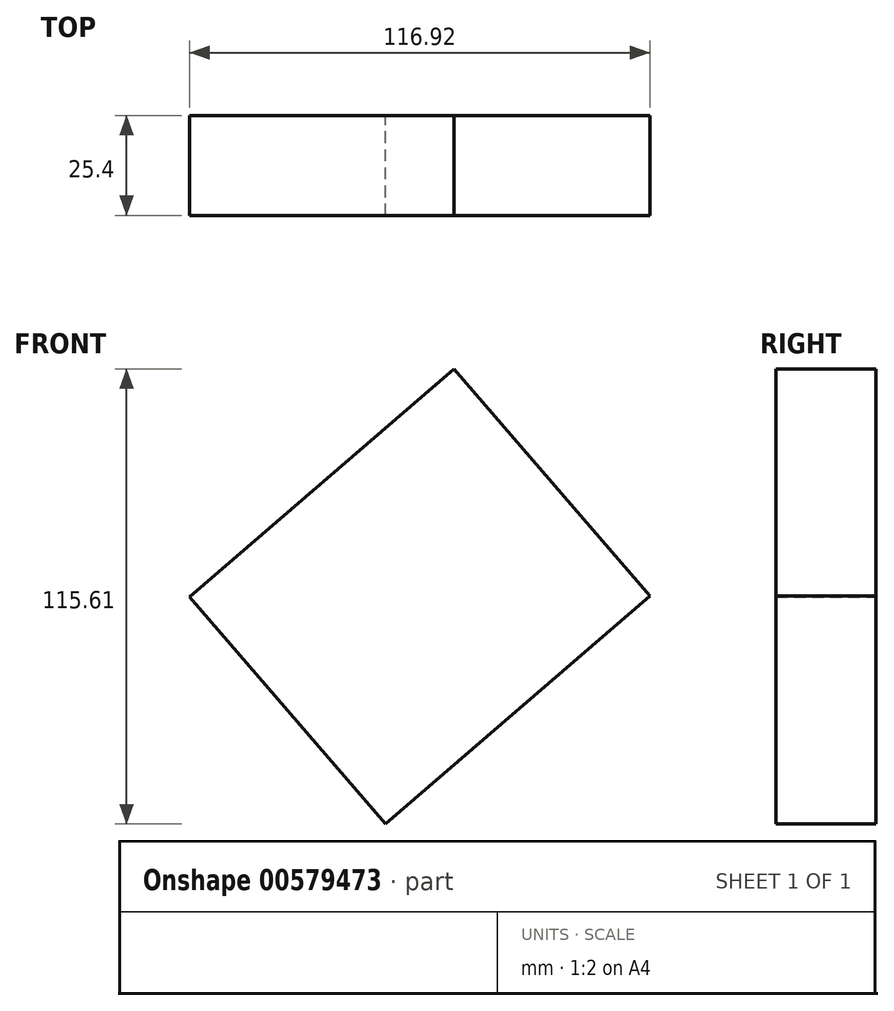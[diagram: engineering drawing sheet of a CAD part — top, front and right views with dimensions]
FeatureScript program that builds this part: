
annotation { "Feature Type Name" : "Feature", "Feature Type Description" : "" }
export const myFeature = defineFeature(function(context is Context, id is Id, definition is map)
    precondition{}
    {
        {
            var Q0;
            Q0=qCreatedBy(makeId("Front.planeOp"),FACE);
            var sketch = newSketch(context, id + "F0", { "sketchPlane" : qUnion([Q0])});
            skLineSegment(sketch, "E0", {"start": v(41.01, 93) * mm, "end": v(90.75, 35.36) * mm});
            skLineSegment(sketch, "E1", {"start": v(90.75, 35.36) * mm, "end": v(157.93, 93.34) * mm});
            skLineSegment(sketch, "E2", {"start": v(157.93, 93.34) * mm, "end": v(108.2, 150.97) * mm});
            skLineSegment(sketch, "E3", {"start": v(108.2, 150.97) * mm, "end": v(41.01, 93) * mm});
            skSolve(sketch);
        }
        {
            var Q0;
            Q0=makeQuery(id+"F0.imprint","IMPRINT",FACE,{"disambiguationData":[TD([[makeQuery(id+"F0.imprint","IMPRINT",EDGE,{"derivedFrom":sQuery(id+"F0.wireOp",EDGE,"E0")}),1.0]])]});
            extrude(context, id + "F1", {"entities" : qUnion([Q0]), "depth" : 25.4 * mm, "offsetDistance" : 25.4 * mm});
        }
    });
